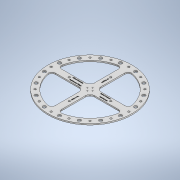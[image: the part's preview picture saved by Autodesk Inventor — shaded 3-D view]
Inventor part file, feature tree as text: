
AUTODESK INVENTOR PART (.ipt)
format: ipt  version: 2020.2 (Build 242310000, 310)  size: 1,961,472 bytes
history: native  units: mm
features: sketch x6, hole x3, extrude x2
ambient origin geometry x8: Origin, YZ Plane, XZ Plane, XY Plane, X Axis, Y Axis, Z Axis, Center Point
bodies: Solido1 (feature_tree)
feature tree (11):
  extrude  "Estrusione1"  Depth=260.0mm
  hole  "Foro1"  [1 undecoded]
  hole  "Foro2"  [1 undecoded]
  hole  "Foro3"  [1 undecoded]
  extrude  "Estrusione2"  Depth=40.0mm TaperAngle=360.0deg
  sketch  "Schizzo 3D1"
  sketch  "Schizzo1"
  sketch  "Schizzo2"
  sketch  "Schizzo3"
  sketch  "Schizzo4"
  sketch  "Schizzo5"
note: 3 required parameter values undecoded (feature->parameter linkage not recoverable at this tier; creation-order binding heuristic only, values carry confidence <= 0.55)
